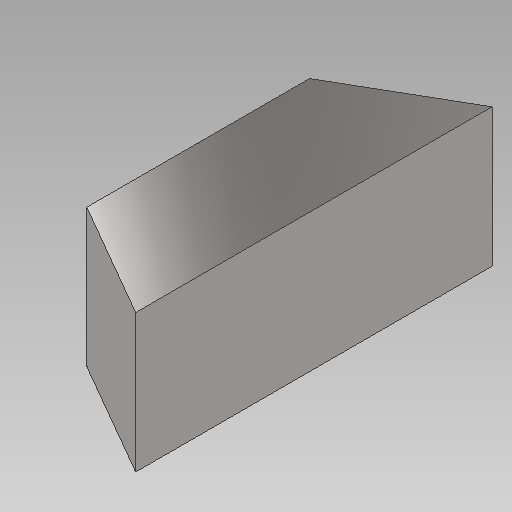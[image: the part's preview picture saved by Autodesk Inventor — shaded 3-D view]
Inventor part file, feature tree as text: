
AUTODESK INVENTOR PART (.ipt)
format: ipt  version: 2020 (Build 240168000, 168)  size: 150,528 bytes
history: native  units: in
note: dims shown in document units (in); Inventor stores cm internally (conversion verified against a paired STEP export)
features: extrude x5, sketch x4
ambient origin geometry x8: Origin, YZ Plane, XZ Plane, XY Plane, X Axis, Y Axis, Z Axis, Center Point
bodies: Solid1 (feature_tree)
feature tree (9):
  extrude  "Extrusion1"  Depth=1.9685in
  extrude  "Extrusion2"  Depth=2.4409in
  extrude  "Extrusion3"  TaperAngle=90.0deg  [1 undecoded]
  sketch  "Sketch4"  dims[d7=2.4409in d8=0.0in d9=0.7874in d10=2.3622in d11=120.0deg d12=0.7874in d13=2.3622in d14=120.0deg d15=2.4409in d16=0.0in d17=2.4409in d18=0.0in d19=2.4409in d20=0.0in]
  extrude  "Extrusion4"  Depth=2.4409in
  extrude  "Extrusion5"  Depth=2.4409in
  sketch  "Sketch1"  dims[d0=1.9685in d1=7.874in]
  sketch  "Sketch2"  dims[d2=2.4409in d3=0.0in d4=1.5748in]
  sketch  "Sketch3"  dims[d5=0.7874in d6=90.0deg]
note: 1 required parameter value undecoded (feature->parameter linkage not recoverable at this tier; creation-order binding heuristic only, values carry confidence <= 0.55)
